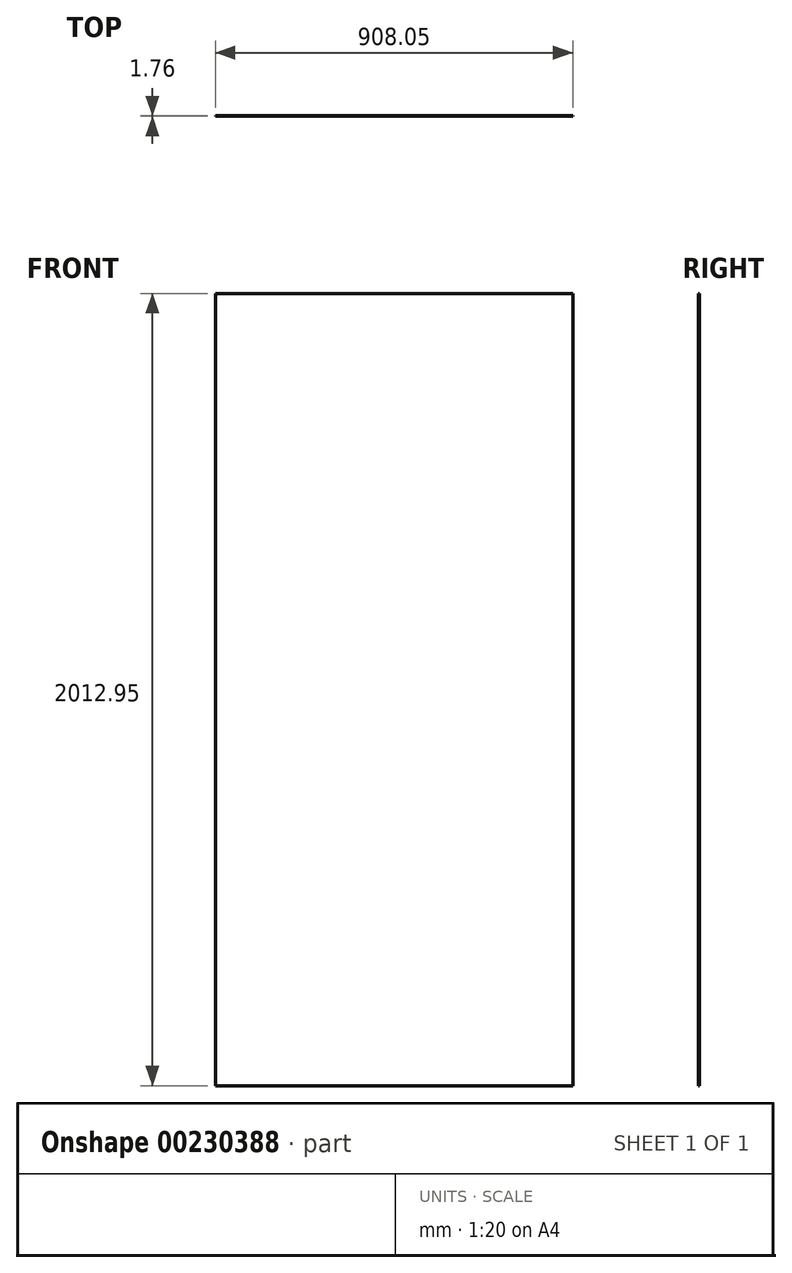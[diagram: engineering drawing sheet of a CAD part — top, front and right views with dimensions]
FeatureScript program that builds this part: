
annotation { "Feature Type Name" : "Feature", "Feature Type Description" : "" }
export const myFeature = defineFeature(function(context is Context, id is Id, definition is map)
    precondition{}
    {
        {
            var Q0;
            Q0=qCreatedBy(makeId("Front.planeOp"),FACE);
            var sketch = newSketch(context, id + "F0", { "sketchPlane" : qUnion([Q0])});
            skLineSegment(sketch, "E0.bottom", {"start": v(0, 0) * mm, "end": v(908.05, 0) * mm});
            skLineSegment(sketch, "E0.top", {"start": v(0, -2012.95) * mm, "end": v(908.05, -2012.95) * mm});
            skLineSegment(sketch, "E0.left", {"start": v(0, 0) * mm, "end": v(0, -2012.95) * mm});
            skLineSegment(sketch, "E0.right", {"start": v(908.05, 0) * mm, "end": v(908.05, -2012.95) * mm});
            skSolve(sketch);
        }
        {
            var Q0;
            Q0 = qSketchRegion(id + "F0", true);
            extrude(context, id + "F1", {"entities" : qUnion([Q0]), "depth" : ((1 + 3 / 4) / 2) * mm, "hasSecondDirection" : true, "secondDirectionOppositeDirection" : true, "secondDirectionDepth" : ((1 + 3 / 4) / 2) * mm});
        }
        {
            var Q0;
            Q0=qCreatedBy(makeId("Front.planeOp"),FACE);
            var sketch = newSketch(context, id + "F2", { "sketchPlane" : qUnion([Q0])});
            skLineSegment(sketch, "E1.bottom", {"start": v(161.04, -114.55) * mm, "end": v(747.01, -114.55) * mm});
            skLineSegment(sketch, "E1.top", {"start": v(161.04, -1041.15) * mm, "end": v(747.01, -1041.15) * mm});
            skLineSegment(sketch, "E1.left", {"start": v(161.04, -114.55) * mm, "end": v(161.04, -1041.15) * mm});
            skLineSegment(sketch, "E1.right", {"start": v(747.01, -114.55) * mm, "end": v(747.01, -1041.15) * mm});
            skLineSegment(sketch, "E2.bottom", {"start": v(161.04, -1213.36) * mm, "end": v(747.01, -1213.36) * mm});
            skLineSegment(sketch, "E2.top", {"start": v(161.04, -1828.8) * mm, "end": v(747.01, -1828.8) * mm});
            skLineSegment(sketch, "E2.left", {"start": v(161.04, -1213.36) * mm, "end": v(161.04, -1828.8) * mm});
            skLineSegment(sketch, "E2.right", {"start": v(747.01, -1213.36) * mm, "end": v(747.01, -1828.8) * mm});
            skLineSegment(sketch, "E3.0", {"start": v(211.84, -165.35) * mm, "end": v(696.21, -165.35) * mm});
            skLineSegment(sketch, "E3.1", {"start": v(211.84, -165.35) * mm, "end": v(211.84, -990.35) * mm});
            skLineSegment(sketch, "E3.2", {"start": v(211.84, -990.35) * mm, "end": v(696.21, -990.35) * mm});
            skLineSegment(sketch, "E3.3", {"start": v(696.21, -165.35) * mm, "end": v(696.21, -990.35) * mm});
            skLineSegment(sketch, "E4.0", {"start": v(211.84, -1264.16) * mm, "end": v(696.21, -1264.16) * mm});
            skLineSegment(sketch, "E4.1", {"start": v(211.84, -1264.16) * mm, "end": v(211.84, -1778) * mm});
            skLineSegment(sketch, "E4.2", {"start": v(211.84, -1778) * mm, "end": v(696.21, -1778) * mm});
            skLineSegment(sketch, "E4.3", {"start": v(696.21, -1264.16) * mm, "end": v(696.21, -1778) * mm});
            skLineSegment(sketch, "E5", {"start": v(211.84, -165.35) * mm, "end": v(161.04, -114.55) * mm});
            skLineSegment(sketch, "E6", {"start": v(696.21, -165.35) * mm, "end": v(747.01, -114.55) * mm});
            skLineSegment(sketch, "E7", {"start": v(696.21, -990.35) * mm, "end": v(747.01, -1041.15) * mm});
            skLineSegment(sketch, "E8", {"start": v(211.84, -990.35) * mm, "end": v(161.04, -1041.15) * mm});
            skLineSegment(sketch, "E9", {"start": v(696.21, -1264.16) * mm, "end": v(747.01, -1213.36) * mm});
            skLineSegment(sketch, "E10", {"start": v(211.84, -1264.16) * mm, "end": v(161.04, -1213.36) * mm});
            skLineSegment(sketch, "E11", {"start": v(211.84, -1778) * mm, "end": v(161.04, -1828.8) * mm});
            skLineSegment(sketch, "E12", {"start": v(747.01, -1828.8) * mm, "end": v(696.21, -1778) * mm});
            skSolve(sketch);
        }
    });
